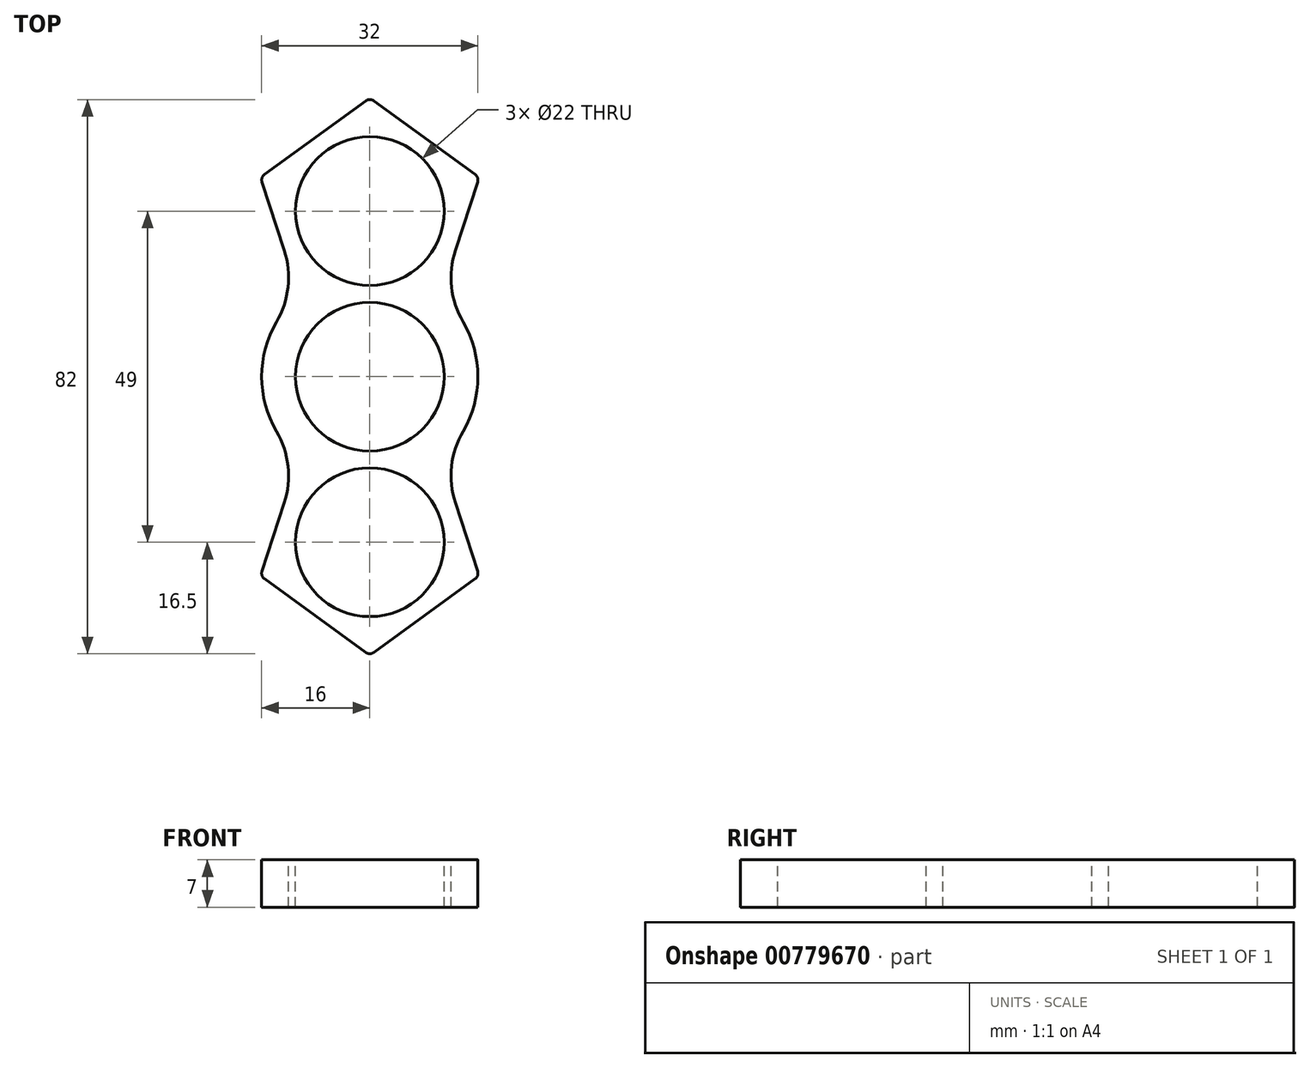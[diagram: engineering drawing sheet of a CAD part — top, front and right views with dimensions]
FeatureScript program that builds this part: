
annotation { "Feature Type Name" : "Feature", "Feature Type Description" : "" }
export const myFeature = defineFeature(function(context is Context, id is Id, definition is map)
    precondition{}
    {
        {
            var Q0;
            Q0=qCreatedBy(makeId("Top.planeOp"),FACE);
            var sketch = newSketch(context, id + "F0", { "sketchPlane" : qUnion([Q0])});
            skArc(sketch, "E0", {"start": v(11, 0) * mm, "mid": v(0, 11) * mm, "end": v(-11, 0) * mm});
            skLineSegment(sketch, "E1", {"start": v(-58.35, 0) * mm, "end": v(58.35, 0) * mm, "construction": true});
            skLineSegment(sketch, "E2", {"start": v(0, 58.35) * mm, "end": v(0, -58.35) * mm, "construction": true});
            skArc(sketch, "E3", {"start": v(-13.8, 8.08) * mm, "mid": v(-15.44, 4.19) * mm, "end": v(-16, 0) * mm});
            skLineSegment(sketch, "E4", {"start": v(-15.95, 28.8) * mm, "end": v(-12.66, 18.67) * mm});
            skLineSegment(sketch, "E5", {"start": v(-15.59, 29.91) * mm, "end": v(-0.59, 40.8) * mm});
            skLineSegment(sketch, "E6.MirrorCS", {"start": v(15.95, 28.8) * mm, "end": v(12.66, 18.67) * mm});
            skLineSegment(sketch, "E7.MirrorCS", {"start": v(15.59, 29.91) * mm, "end": v(0.59, 40.8) * mm});
            skPoint(sketch, "E8.visualSharp", {"position": v(-16.18, 29.48) * mm});
            skArc(sketch, "E8.filletArc", {"start": v(-15.59, 29.91) * mm, "mid": v(-15.95, 29.41) * mm, "end": v(-15.95, 28.8) * mm});
            skPoint(sketch, "E9.visualSharp", {"position": v(0, 41.24) * mm});
            skArc(sketch, "E9.filletArc", {"start": v(0.59, 40.8) * mm, "mid": v(0, 41) * mm, "end": v(-0.59, 40.8) * mm});
            skPoint(sketch, "E10.visualSharp", {"position": v(16.18, 29.48) * mm});
            skArc(sketch, "E10.filletArc", {"start": v(15.95, 28.8) * mm, "mid": v(15.95, 29.41) * mm, "end": v(15.59, 29.91) * mm});
            skArc(sketch, "E11", {"start": v(-13.8, 8.08) * mm, "mid": v(-12.1, 13.25) * mm, "end": v(-12.66, 18.67) * mm});
            skPoint(sketch, "E12.orphan", {"position": v(-10.85, 13.1) * mm});
            skArc(sketch, "E13.MirrorCS", {"start": v(13.8, 8.08) * mm, "mid": v(12.1, 13.25) * mm, "end": v(12.66, 18.67) * mm});
            skPoint(sketch, "E14.orphan", {"position": v(10.85, 13.1) * mm});
            skArc(sketch, "E15.trimOffspring", {"start": v(16, 0) * mm, "mid": v(15.44, 4.19) * mm, "end": v(13.8, 8.08) * mm});
            skLineSegment(sketch, "E16", {"start": v(-11, 0) * mm, "end": v(-16, 0) * mm});
            skLineSegment(sketch, "E17", {"start": v(11, 0) * mm, "end": v(16, 0) * mm});
            skSolve(sketch);
        }
        {
            var Q0;
            Q0 = qSketchRegion(id + "F0", true);
            extrude(context, id + "F1", {"entities" : qUnion([Q0]), "endBound" : BoundingType.SYMMETRIC, "oppositeDirection" : true, "depth" : 7 * mm, "offsetDistance" : 25 * mm});
        }
        {
            var Q0;
            Q0=makeQuery(id+"F1.opExtrude","SWEPT_BODY",BODY,{"disambiguationData":[OSD([sQuery(id+"F0.wireOp",EDGE,"E0"),sQuery(id+"F0.wireOp",EDGE,"E3"),sQuery(id+"F0.wireOp",EDGE,"E4"),sQuery(id+"F0.wireOp",EDGE,"E5"),sQuery(id+"F0.wireOp",EDGE,"E6.MirrorCS"),sQuery(id+"F0.wireOp",EDGE,"E7.MirrorCS"),sQuery(id+"F0.wireOp",EDGE,"E8.filletArc"),sQuery(id+"F0.wireOp",EDGE,"E9.filletArc"),sQuery(id+"F0.wireOp",EDGE,"E10.filletArc"),sQuery(id+"F0.wireOp",EDGE,"E11"),sQuery(id+"F0.wireOp",EDGE,"E13.MirrorCS"),sQuery(id+"F0.wireOp",EDGE,"E15.trimOffspring"),sQuery(id+"F0.wireOp",EDGE,"E16"),sQuery(id+"F0.wireOp",EDGE,"E17")])]});
            var Q1;
            Q1=makeQuery(id+"F1.opExtrude","SWEPT_FACE",FACE,{"disambiguationData":[OSD([sQuery(id+"F0.wireOp",EDGE,"E16")])]});
            mirror(context, id + "F2", {"operationType" : NewBodyOperationType.ADD, "entities" : qUnion([Q0]), "mirrorPlane" : qUnion([Q1])});
        }
        {
            var Q0;
            {var subQ0=makeQuery(id+"F1.opExtrude","CAP_FACE",FACE,{"disambiguationData":[OSD([sQuery(id+"F0.wireOp",EDGE,"E0"),sQuery(id+"F0.wireOp",EDGE,"E3"),sQuery(id+"F0.wireOp",EDGE,"E4"),sQuery(id+"F0.wireOp",EDGE,"E5"),sQuery(id+"F0.wireOp",EDGE,"E6.MirrorCS"),sQuery(id+"F0.wireOp",EDGE,"E7.MirrorCS"),sQuery(id+"F0.wireOp",EDGE,"E8.filletArc"),sQuery(id+"F0.wireOp",EDGE,"E9.filletArc"),sQuery(id+"F0.wireOp",EDGE,"E10.filletArc"),sQuery(id+"F0.wireOp",EDGE,"E11"),sQuery(id+"F0.wireOp",EDGE,"E13.MirrorCS"),sQuery(id+"F0.wireOp",EDGE,"E15.trimOffspring"),sQuery(id+"F0.wireOp",EDGE,"E16"),sQuery(id+"F0.wireOp",EDGE,"E17")])],"isStart":true});Q0=makeQuery(id+"F2.boolean.opBoolean","MERGE",FACE,{"derivedFrom":[subQ0,makeQuery(id+"F2.opPattern","COPY",FACE,{"derivedFrom":subQ0,"instanceName":"1"})]});}
            var sketch = newSketch(context, id + "F3", { "sketchPlane" : qUnion([Q0])});
            skCircle(sketch, "E18", {"center": v(0, 24.5) * mm, "radius": 11 * mm});
            skLineSegment(sketch, "E19", {"start": v(0, 0) * mm, "end": v(0, 24.5) * mm, "construction": true});
            skLineSegment(sketch, "E20", {"start": v(-11, 0) * mm, "end": v(11, 0) * mm, "construction": true});
            skCircle(sketch, "E21.MirrorC", {"center": v(0, -24.5) * mm, "radius": 11 * mm});
            skSolve(sketch);
        }
        {
            var Q0;
            Q0 = qSketchRegion(id + "F3", true);
            extrude(context, id + "F4", {"entities" : qUnion([Q0]), "operationType" : NewBodyOperationType.REMOVE, "endBound" : BoundingType.THROUGH_ALL, "oppositeDirection" : true, "depth" : 25 * mm, "offsetDistance" : 25 * mm});
        }
    });
